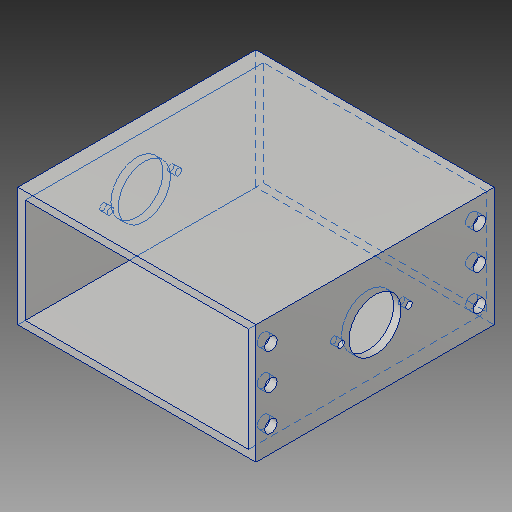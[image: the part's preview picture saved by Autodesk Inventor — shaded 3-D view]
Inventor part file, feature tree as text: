
AUTODESK INVENTOR PART (.ipt)
format: ipt  version: 2019 (Build 230136000, 136)  size: 144,384 bytes
history: native  units: in
note: dims shown in document units (in); Inventor stores cm internally (conversion verified against a paired STEP export)
features: extrude x4, sketch x4
ambient origin geometry x8: Origin, YZ Plane, XZ Plane, XY Plane, X Axis, Y Axis, Z Axis, Center Point
bodies: Solid1 (feature_tree)
feature tree (8):
  extrude  "Extrusion1"  Depth=0.125in
  extrude  "Extrusion3"  Depth=4.0in
  extrude  "Extrusion4"  Depth=0.6in
  extrude  "Extrusion5"  Depth=4.0in
  sketch  "Sketch1"  dims[d0=2.0in d1=0.125in]
  sketch  "Sketch2"  dims[d2=4.0in d3=0.0in d4=0.21in]
  sketch  "Sketch3"  dims[d5=0.25in d6=0.6in]
  sketch  "Sketch4"  dims[d9=1.0in d10=0.0in d11=4.0in d12=0.125in d13=0.875in d14=1.0in d15=0.0in d16=1.0in d17=0.14in d18=0.11in d19=1.0in d20=0.0in]
